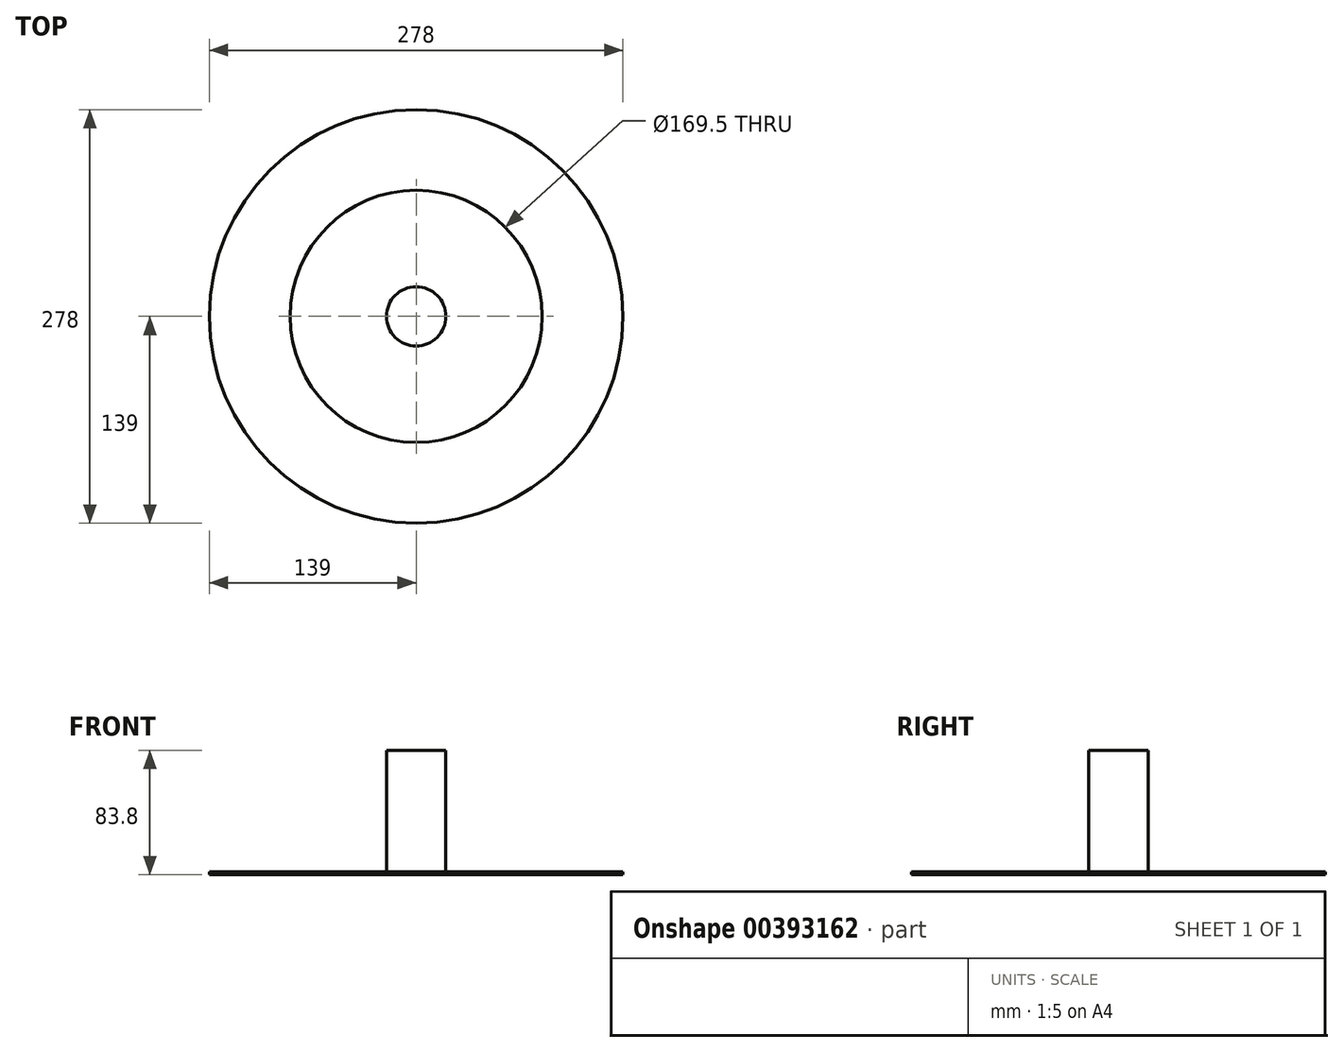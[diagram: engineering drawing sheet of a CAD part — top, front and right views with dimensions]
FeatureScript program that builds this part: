
annotation { "Feature Type Name" : "Feature", "Feature Type Description" : "" }
export const myFeature = defineFeature(function(context is Context, id is Id, definition is map)
    precondition{}
    {
        {
            var Q0;
            Q0=qCreatedBy(makeId("Front.planeOp"),FACE);
            var sketch = newSketch(context, id + "F0", { "sketchPlane" : qUnion([Q0])});
            skLineSegment(sketch, "E0.bottom", {"start": v(0, 0) * mm, "end": v(-139, 0) * mm});
            skLineSegment(sketch, "E0.top", {"start": v(0, 83.8) * mm, "end": v(-139, 83.8) * mm});
            skLineSegment(sketch, "E0.left", {"start": v(0, 0) * mm, "end": v(0, 83.8) * mm});
            skLineSegment(sketch, "E0.right", {"start": v(-139, 0) * mm, "end": v(-139, 83.8) * mm});
            skLineSegment(sketch, "E1.bottom", {"start": v(0, 0) * mm, "end": v(-19.94, 0) * mm});
            skLineSegment(sketch, "E1.top", {"start": v(0, 83.8) * mm, "end": v(-19.94, 83.8) * mm});
            skLineSegment(sketch, "E1.right", {"start": v(-19.94, 0) * mm, "end": v(-19.94, 83.8) * mm});
            skLineSegment(sketch, "E2.bottom", {"start": v(-139, 83.8) * mm, "end": v(-24.23, 83.8) * mm});
            skLineSegment(sketch, "E2.top", {"start": v(-139, 63.8) * mm, "end": v(-24.23, 63.8) * mm});
            skLineSegment(sketch, "E2.left", {"start": v(-139, 83.8) * mm, "end": v(-139, 63.8) * mm});
            skLineSegment(sketch, "E2.right", {"start": v(-24.23, 83.8) * mm, "end": v(-24.23, 63.8) * mm});
            skLineSegment(sketch, "E3.bottom", {"start": v(-139, 83.8) * mm, "end": v(-84.75, 83.8) * mm});
            skLineSegment(sketch, "E3.top", {"start": v(-139, 11.5) * mm, "end": v(-84.75, 11.5) * mm});
            skLineSegment(sketch, "E3.left", {"start": v(-139, 83.8) * mm, "end": v(-139, 11.5) * mm});
            skLineSegment(sketch, "E3.right", {"start": v(-84.75, 83.8) * mm, "end": v(-84.75, 11.5) * mm});
            skLineSegment(sketch, "E4.bottom", {"start": v(-139, 0) * mm, "end": v(-84.75, 0) * mm});
            skLineSegment(sketch, "E4.top", {"start": v(-139, 2) * mm, "end": v(-84.75, 2) * mm});
            skLineSegment(sketch, "E4.left", {"start": v(-139, 0) * mm, "end": v(-139, 2) * mm});
            skLineSegment(sketch, "E4.right", {"start": v(-84.75, 0) * mm, "end": v(-84.75, 2) * mm});
            skSolve(sketch);
        }
        {
            var Q0;
            Q0=makeQuery(id+"F0.imprint","IMPRINT",FACE,{"disambiguationData":[TD([[makeQuery(id+"F0.imprint","IMPRINT",EDGE,{"derivedFrom":sQuery(id+"F0.wireOp",EDGE,"E0.bottom")}),-1.0]])]});
            var Q1;
            Q1=sQuery(id+"F0.wireOp",EDGE,"E0.left");
            revolve(context, id + "F1", {"entities" : qUnion([Q0]), "axis" : qUnion([Q1]), "revolveType" : RevolveType.FULL});
        }
        {
            var Q0;
            Q0=qCreatedBy(makeId("Top.planeOp"),FACE);
            var sketch = newSketch(context, id + "F2", { "sketchPlane" : qUnion([Q0])});
            skCircle(sketch, "E5", {"center": v(0, 0) * mm, "radius": 65 * mm, "construction": true});
            skCircle(sketch, "E6", {"center": v(64.96, -2.36) * mm, "radius": 7 * mm});
            skCircle(sketch, "E7.1.0", {"center": v(2.36, 64.96) * mm, "radius": 7 * mm});
            skCircle(sketch, "E7.2.0", {"center": v(-64.96, 2.36) * mm, "radius": 7 * mm});
            skCircle(sketch, "E7.3.0", {"center": v(-2.36, -64.96) * mm, "radius": 7 * mm});
            skSolve(sketch);
        }
        {
            var Q0;
            Q0 = qSketchRegion(id + "F2", true);
            extrude(context, id + "F3", {"entities" : qUnion([Q0]), "operationType" : NewBodyOperationType.REMOVE, "depth" : 61.8 * mm});
        }
    });
